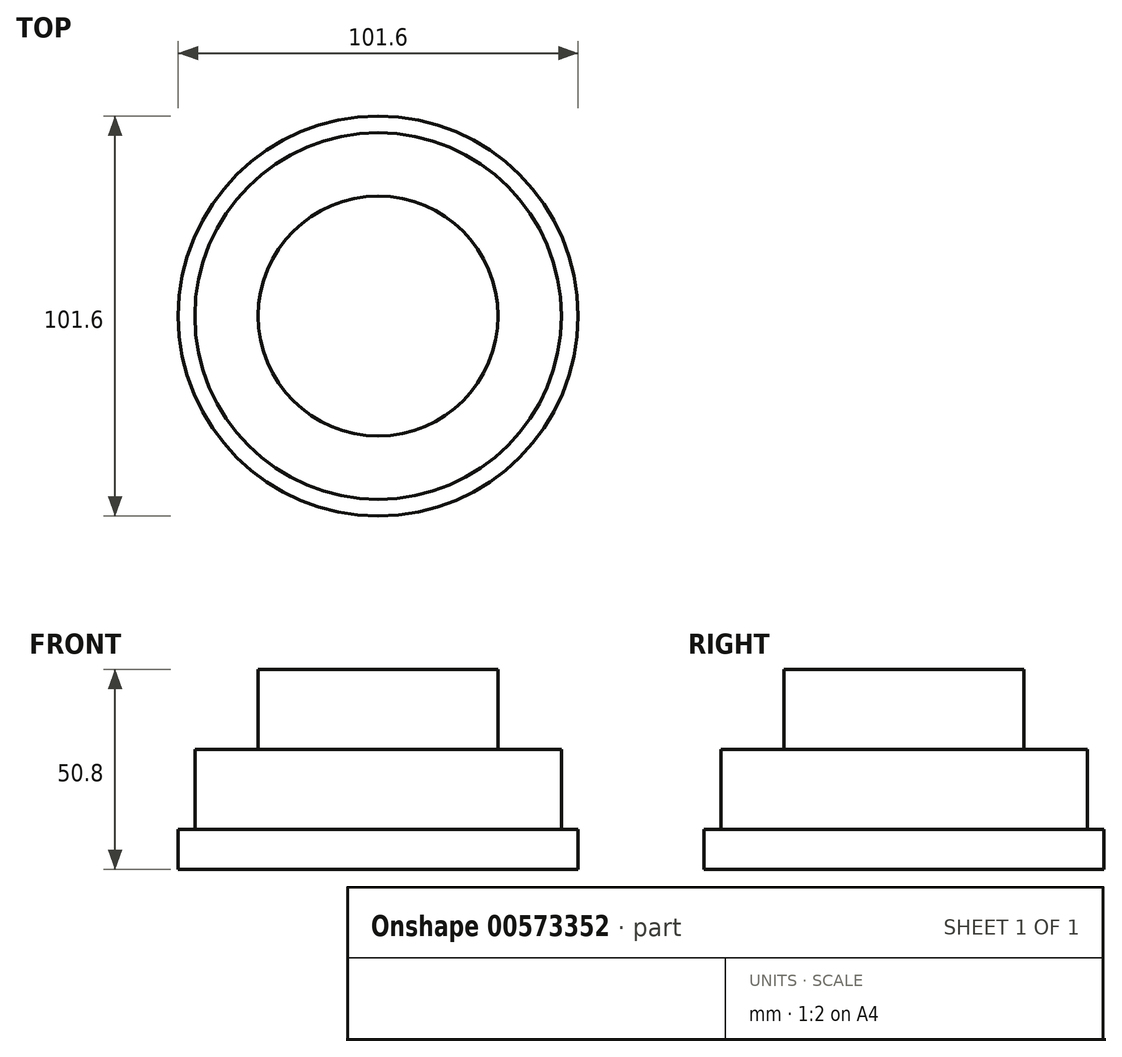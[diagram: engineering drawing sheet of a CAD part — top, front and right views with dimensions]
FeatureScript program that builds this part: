
annotation { "Feature Type Name" : "Feature", "Feature Type Description" : "" }
export const myFeature = defineFeature(function(context is Context, id is Id, definition is map)
    precondition{}
    {
        {
            var Q0;
            Q0=qCreatedBy(makeId("Top.planeOp"),FACE);
            var sketch = newSketch(context, id + "F0", { "sketchPlane" : qUnion([Q0])});
            skCircle(sketch, "E0", {"center": v(0, 0) * mm, "radius": 50.8 * mm});
            skSolve(sketch);
        }
        {
            var Q0;
            Q0 = qSketchRegion(id + "F0", true);
            var Q1;
            Q1 = qSketchRegion(id + "F2", true);
            extrude(context, id + "F1", {"entities" : qUnion([Q0, Q1]), "depth" : 10.16 * mm, "offsetDistance" : 25.4 * mm});
        }
        {
            var Q0;
            Q0=makeQuery(id+"F1.opExtrude","CAP_FACE",FACE,{"disambiguationData":[OSD([sQuery(id+"F0.wireOp",EDGE,"E0")])],"isStart":false});
            var sketch = newSketch(context, id + "F2", { "sketchPlane" : qUnion([Q0])});
            skCircle(sketch, "E1", {"center": v(0, 0) * mm, "radius": 46.57 * mm});
            skSolve(sketch);
        }
        {
            var Q0;
            Q0 = qSketchRegion(id + "F2", true);
            extrude(context, id + "F3", {"entities" : qUnion([Q0]), "operationType" : NewBodyOperationType.ADD, "depth" : 20.32 * mm, "offsetDistance" : 25.4 * mm});
        }
        {
            var Q0;
            Q0=makeQuery(id+"F3.opExtrude","CAP_FACE",FACE,{"disambiguationData":[OSD([sQuery(id+"F2.wireOp",EDGE,"E1")])],"isStart":false});
            var sketch = newSketch(context, id + "F4", { "sketchPlane" : qUnion([Q0])});
            skCircle(sketch, "E2", {"center": v(0, 0) * mm, "radius": 30.48 * mm});
            skSolve(sketch);
        }
        {
            var Q0;
            Q0 = qSketchRegion(id + "F4", true);
            extrude(context, id + "F5", {"entities" : qUnion([Q0]), "operationType" : NewBodyOperationType.ADD, "depth" : 20.32 * mm, "offsetDistance" : 25.4 * mm});
        }
    });
